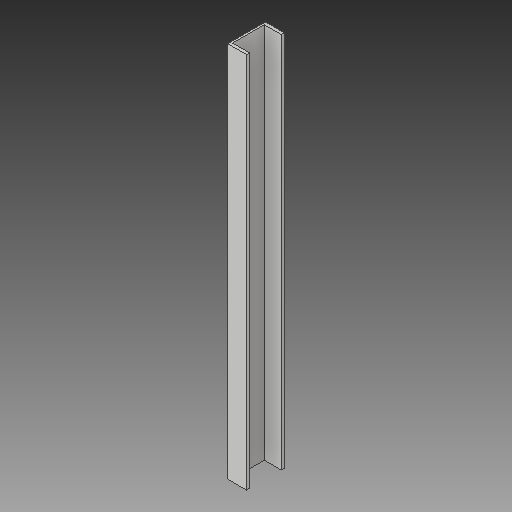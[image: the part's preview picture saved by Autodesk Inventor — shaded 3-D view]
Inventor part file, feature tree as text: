
AUTODESK INVENTOR PART (.ipt)
format: ipt  version: 2019 (Build 230136000, 136)  size: 90,112 bytes
history: native  units: in
note: dims shown in document units (in); Inventor stores cm internally (conversion verified against a paired STEP export)
features: other x3, sketch x1
ambient origin geometry x8: Origin, YZ Plane, XZ Plane, XY Plane, X Axis, Y Axis, Z Axis, Center Point
bodies: Solid1 (feature_tree)
feature tree (4):
  other  "Channel1_MIR1.ipt"
  other  "Solid1::Channel1_MIR1.ipt"
  other  "TaggingFeature1"
  sketch  "Sketch1"  dims[d0=0.3937in]
